# Revit family: FT 703020001_Válvula para Orinal Push Entrada Posterior Empotrada
name_source: partatom
category: Plumbing Fixtures
units: mm (PartAtom-declared; Revit-internal decimal feet)

## family parameters
Always vertical = Yes
Cut with Voids When Loaded = No
Host = Wall
OmniClass Number = 23.31.11.00
OmniClass Title = Faucets
Part Type = Normal
Room Calculation Point = No
Round Connector Dimension = Use Diameter
Shared = No

## types (1)
- Válvula Push
    Capacidad de flujo estimada real = 6,35 - 9,68 L/min - 0,33 - 0,49 L/Descarga
    Capacidad de flujo máximo por norma = 9,68 L/min - 0,49 L/Descarga.
    Creado por = IDD
    Description = Las válvulas para orinal Corona son el aliado perfecto para las necesidades de las
instituciones de alto tráfico, están diseñadas para un óptimo funcionamiento y
durabilidad debido a sus características antivandálicas.
• Válvula empotrada de accionamiento automático tipo Push.
• Consumo de agua desde 0.5 L hasta 1.9 L.
• Cierre automático temporizado entre 4 y 7 segundos.
• Diseño adecuado con un grado elevado de antivandalismo para tráfico alto.
    Fecha de creación = 12/08/2020
    Garantía = 3 años
    Garantía Acabados = 2 Años
    Manufacturer = Corona
    Model = Válvula Push
    Peso Bruto aprox = 900g 1,98lb.
    Peso Neto aprox = 795g 1,75lb.
    Presion maxima = 80 Psi
    Presion minima = 20 Psi.
    Presión de trabajo = 20 - 80 Psi.
    Referencia = 703020001
    URL = https://corona.co
    Vida útil de la unidad de cierre = 150 Mil Ciclos
